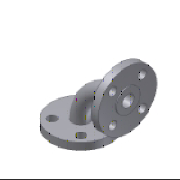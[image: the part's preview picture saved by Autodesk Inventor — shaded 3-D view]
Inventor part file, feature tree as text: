
AUTODESK INVENTOR PART (.ipt)
format: ipt  version: 2023.2 (Build 272271030, 271C)  size: 332,800 bytes
history: native  units: mm (DEFAULTED — no unit token found)
features: sketch x5, other x4, revolve x2, extrude x2, pattern_circular x2, sweep x1
ambient origin geometry x8: Origin, YZ Plane, XZ Plane, XY Plane, X Axis, Y Axis, Z Axis, Center Point
bodies: Solid1 (feature_tree)
feature tree (16):
  sketch  "Sketch1"  dims[d0=432.0mm d1=710.0mm]
  revolve  "Revolution1"  [1 undecoded]
  revolve  "Revolution2"  [1 undecoded]
  sweep  "Sweep1"
  extrude  "Extrusion1"  Depth=60.5mm
  pattern_circular  "Circular Pattern1"  [2 undecoded]
  extrude  "Extrusion2"  Depth=710.0mm
  pattern_circular  "Circular Pattern2"  [2 undecoded]
  other  "Work Point1"
  other  "Work Point2"
  other  "Work Axis1"
  other  "Work Axis2"
  sketch  "Sketch2"  dims[d2=533.5mm d3=2.0mm]
  sketch  "Sketch3"  dims[d4=60.5mm d5=90.0deg]
  sketch  "Sketch6"  dims[d6=2.0mm d7=60.5mm]
  sketch  "Sketch7"  dims[d8=432.0mm d9=533.5mm d10=710.0mm d11=457.0mm d12=457.0mm d13=90.0deg d14=470.0mm d15=0.0mm d16=240.0mm d17=360.0deg d18=240.0mm d19=360.0deg d20=1.308997mm d21=35.5mm d22=628.5mm d34=25.4mm d24=0.0mm d25=1.308997mm d26=35.5mm d27=628.5mm d39=25.4mm d28=0.0mm d41=0.0mm]
note: 6 required parameter values undecoded (feature->parameter linkage not recoverable at this tier; creation-order binding heuristic only, values carry confidence <= 0.55)